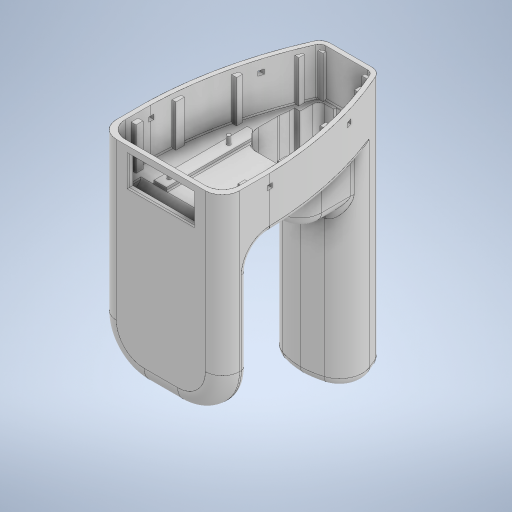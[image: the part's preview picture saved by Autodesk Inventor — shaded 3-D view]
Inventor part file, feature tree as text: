
AUTODESK INVENTOR PART (.ipt)
format: ipt  version: 2023 (Build 270158000, 158)  size: 1,034,752 bytes
history: native  units: in
note: dims shown in document units (in); Inventor stores cm internally (conversion verified against a paired STEP export)
features: extrude x19, sketch x19, fillet x7, chamfer x5, projected_geometry x4, plane x3, mirror x1
ambient origin geometry x8: Origin, YZ Plane, XZ Plane, XY Plane, X Axis, Y Axis, Z Axis, Center Point
bodies: Body1 (feature_tree)
feature tree (58):
  extrude  "Extrusion4"  Depth=3.5433in
  plane  "Work Plane1"
  extrude  "Extrusion5"  Depth=0.4331in TaperAngle=0.0deg
  extrude  "Extrusion6"  Depth=1.5906in
  extrude  "Extrusion7"  Depth=0.7972in
  extrude  "Extrusion8"  Depth=0.0866in TaperAngle=0.0deg
  extrude  "Extrusion9"  Depth=0.2362in TaperAngle=0.0deg
  extrude  "Extrusion10"  Depth=0.0787in
  fillet  "Fillet2"  Radius=0.0787in
  chamfer  "Chamfer1"  Distance=1.0487in
  extrude  "Extrusion11"  Depth=0.4921in TaperAngle=0.0deg
  fillet  "Fillet3"  Radius=1.1417in
  extrude  "Extrusion12"  Depth=0.5709in
  extrude  "Extrusion13"  Depth=0.3937in TaperAngle=0.0deg
  chamfer  "Chamfer2"  Distance=0.0787in
  chamfer  "Chamfer3"  Distance=0.125in Angle=45.0deg
  chamfer  "Chamfer4"  Distance=0.0629in
  extrude  "Extrusion15"  Depth=0.0787in
  fillet  "Fillet7"  Radius=0.0629in
  extrude  "Extrusion16"  Depth=1.048in
  extrude  "Extrusion17"  Depth=0.37in
  fillet  "Fillet8"  Radius=0.22in
  plane  "Work Plane3"
  extrude  "Extrusion19"  Depth=0.25in
  plane  "Work Plane4"
  extrude  "Extrusion20"  Depth=0.25in
  mirror  "Mirror1"
  extrude  "Extrusion21"  Depth=0.25in
  extrude  "Extrusion22"  Depth=0.25in TaperAngle=0.0deg
  fillet  "Fillet10"  Radius=0.02in
  fillet  "Fillet11"  Radius=0.02in
  extrude  "Extrusion23"  Depth=0.25in TaperAngle=45.0deg
  extrude  "Extrusion24"  Depth=0.25in TaperAngle=0.0deg
  fillet  "Fillet12"  Radius=0.1in
  chamfer  "Chamfer5"  Distance=1.0in
  sketch  "Sketch4"  dims[d10=2.1654in d11=3.5433in]
  sketch  "Sketch5"  dims[d12=0.7874in d13=0.4331in d14=0.0in]
  sketch  "Sketch6"  dims[d16=-0.2835in d17=1.5906in]
  sketch  "Sketch7"  dims[d18=2.3819in d19=0.7972in]
  sketch  "Sketch8"  dims[d20=0.338in d21=0.0866in d22=0.0in]
  sketch  "Sketch9"  dims[d23=0.7874in d24=0.2362in d25=0.0in]
  sketch  "Sketch10"  dims[d26=0.0787in d27=0.0787in d28=0.0787in d29=1.0487in d30=0.0in]
  sketch  "Sketch11"  dims[d31=0.0591in d32=0.4921in d33=0.0in d34=1.1417in]
  sketch  "Sketch12"  dims[d35=0.5118in d36=0.5709in]
  projected_geometry  "Projected Loop1"
  sketch  "Sketch13"  dims[d37=0.126in d38=0.3937in d39=0.0in]
  sketch  "Sketch15"  dims[d40=0.3937in]
  projected_geometry  "Projected Loop2"
  sketch  "Sketch17"  dims[d41=0.3937in]
  projected_geometry  "Projected Loop3"
  sketch  "Sketch18"  dims[d42=3.3465in]
  sketch  "Sketch21"  dims[d43=0.1969in d44=0.0787in d45=0.0in]
  sketch  "Sketch22"  dims[d46=0.4in d47=0.125in d48=0.125in d49=45.0deg d52=0.0629in d53=0.0in]
  sketch  "Sketch23"  dims[d54=0.3in d56=0.0787in d57=0.0629in d58=0.0in]
  sketch  "Sketch25"  dims[d59=0.9685in d60=1.048in]
  sketch  "Sketch26"  dims[d62=0.6299in d63=0.37in d64=0.22in]
  projected_geometry  "Projected Loop6"
  sketch  "Sketch27"  dims[d65=0.065in d66=0.065in d67=0.065in d68=0.065in d69=0.1378in d70=0.0in d80=0.02in d81=0.125in d82=45.0deg d83=0.02in d84=0.125in d85=45.0deg d86=0.02in d87=0.125in d88=45.0deg d92=3.5433in d93=0.0in d96=0.1in d97=1.0in d98=0.0787in d99=0.0984in d100=0.5in d101=0.1in d102=3.5433in d103=0.0in d104=0.0in d105=0.0in d106=0.15in d107=0.2092in d108=0.2929in d109=0.11in d115=0.4843in d116=0.0866in d117=0.0787in d118=0.0866in d119=0.0787in d120=0.246in d121=0.246in d122=1.575in d123=0.806in d124=0.0in d125=0.0in d126=-0.0874in d127=1.0in d128=0.0in d130=0.21in d131=1.1811in d132=0.0in d134=0.0in d136=0.8in d137=0.0in d139=1.52in d140=0.38in d141=0.18in d142=0.315in d143=0.8in d144=0.0in d145=0.0787in d146=0.063in d147=0.25in d148=0.8711in d149=0.0in d150=0.06in d151=0.025in d152=0.125in d153=45.0deg d94=0.5in d95=0.0344in]
